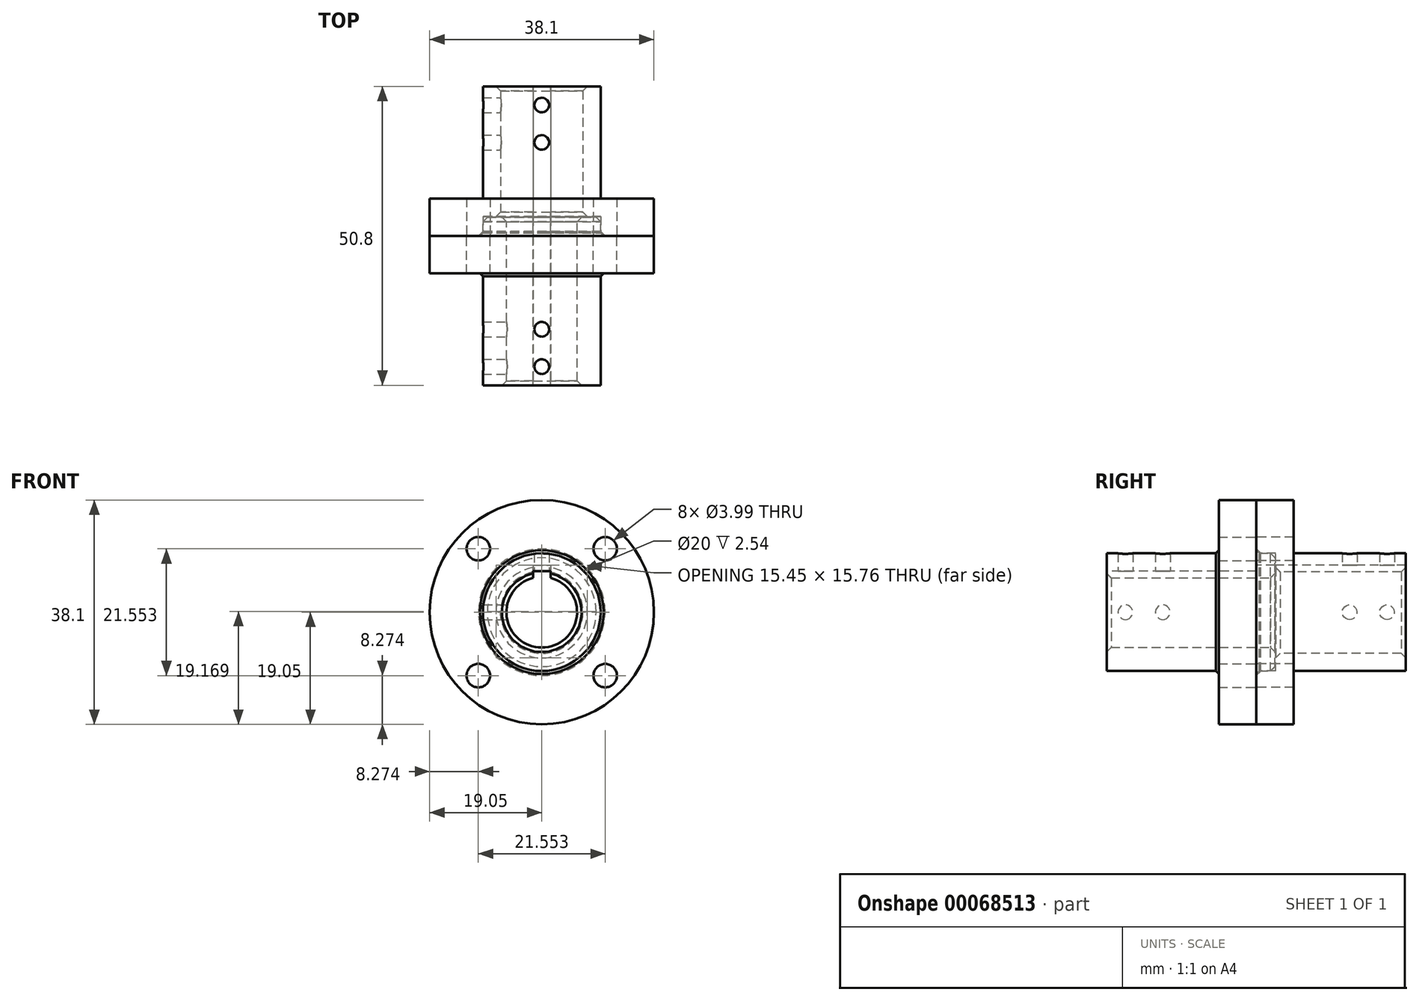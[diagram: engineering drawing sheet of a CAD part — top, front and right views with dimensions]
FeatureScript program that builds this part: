
annotation { "Feature Type Name" : "Feature", "Feature Type Description" : "" }
export const myFeature = defineFeature(function(context is Context, id is Id, definition is map)
    precondition{}
    {
        {
            var Q0;
            Q0=qCreatedBy(makeId("Front.planeOp"),FACE);
            var sketch = newSketch(context, id + "F0", { "sketchPlane" : qUnion([Q0])});
            skCircle(sketch, "E0", {"center": v(0, 0) * mm, "radius": 7 * mm});
            skCircle(sketch, "E1", {"center": v(0, 0) * mm, "radius": 6 * mm});
            skCircle(sketch, "E2", {"center": v(0, 0) * mm, "radius": 19.05 * mm});
            skCircle(sketch, "E3", {"center": v(-10.78, 10.78) * mm, "radius": 2 * mm});
            skCircle(sketch, "E4.1.0", {"center": v(-10.78, -10.78) * mm, "radius": 2 * mm});
            skCircle(sketch, "E4.2.0", {"center": v(10.78, -10.78) * mm, "radius": 2 * mm});
            skCircle(sketch, "E4.3.0", {"center": v(10.78, 10.78) * mm, "radius": 2 * mm});
            skCircle(sketch, "E5", {"center": v(0, 0) * mm, "radius": 10 * mm});
            skSolve(sketch);
        }
        {
            var Q0;
            Q0=qCreatedBy(makeId("Front.planeOp"),FACE);
            var sketch = newSketch(context, id + "F1", { "sketchPlane" : qUnion([Q0])});
            skLineSegment(sketch, "E6.bottom", {"start": v(0, 8) * mm, "end": v(-1.5, 8) * mm});
            skLineSegment(sketch, "E6.top", {"start": v(0, 3.58) * mm, "end": v(-1.5, 3.58) * mm});
            skLineSegment(sketch, "E6.left", {"start": v(0, 8) * mm, "end": v(0, 3.58) * mm, "construction": true});
            skLineSegment(sketch, "E6.right", {"start": v(-1.5, 8) * mm, "end": v(-1.5, 3.58) * mm});
            skLineSegment(sketch, "E7.MirrorCS", {"start": v(0, 8) * mm, "end": v(1.5, 8) * mm});
            skLineSegment(sketch, "E8.MirrorCS", {"start": v(1.5, 8) * mm, "end": v(1.5, 3.58) * mm});
            skLineSegment(sketch, "E9.MirrorCS", {"start": v(0, 3.58) * mm, "end": v(1.5, 3.58) * mm});
            skLineSegment(sketch, "E10", {"start": v(-1.5, 7) * mm, "end": v(1.5, 7) * mm});
            skSolve(sketch);
        }
        {
            var Q0;
            Q0=makeQuery(id+"F0.imprint","IMPRINT",FACE,{"disambiguationData":[TD([[makeQuery(id+"F0.imprint","IMPRINT",EDGE,{"derivedFrom":sQuery(id+"F0.wireOp",EDGE,"E0")}),-1.0]])]});
            var Q1;
            Q1=makeQuery(id+"F0.imprint","IMPRINT",FACE,{"disambiguationData":[TD([[makeQuery(id+"F0.imprint","IMPRINT",EDGE,{"derivedFrom":sQuery(id+"F0.wireOp",EDGE,"E2")}),1.0]])]});
            extrude(context, id + "F2", {"entities" : qUnion([Q0, Q1]), "depth" : 6.35 * mm});
        }
        {
            var Q0;
            Q0=makeQuery(id+"F0.imprint","IMPRINT",FACE,{"disambiguationData":[TD([[makeQuery(id+"F0.imprint","IMPRINT",EDGE,{"derivedFrom":sQuery(id+"F0.wireOp",EDGE,"E0")}),-1.0]])]});
            var Q1;
            Q1=makeQuery(id+"F0.imprint","IMPRINT",FACE,{"disambiguationData":[TD([[makeQuery(id+"F0.imprint","IMPRINT",EDGE,{"derivedFrom":sQuery(id+"F0.wireOp",EDGE,"E0")}),1.0]])]});
            extrude(context, id + "F3", {"entities" : qUnion([Q0, Q1]), "operationType" : NewBodyOperationType.ADD, "depth" : 25.4 * mm, "hasSecondDirection" : true, "secondDirectionOppositeDirection" : true, "secondDirectionDepth" : 3.17 * mm});
        }
        {
            var Q0;
            Q0=makeQuery(id+"F0.imprint","IMPRINT",FACE,{"disambiguationData":[TD([[makeQuery(id+"F0.imprint","IMPRINT",EDGE,{"derivedFrom":sQuery(id+"F0.wireOp",EDGE,"E2")}),1.0]])]});
            extrude(context, id + "F4", {"entities" : qUnion([Q0]), "oppositeDirection" : true, "depth" : 6.35 * mm});
        }
        {
            var Q0;
            Q0=makeQuery(id+"F0.imprint","IMPRINT",FACE,{"disambiguationData":[TD([[makeQuery(id+"F0.imprint","IMPRINT",EDGE,{"derivedFrom":sQuery(id+"F0.wireOp",EDGE,"E0")}),-1.0]])]});
            extrude(context, id + "F5", {"entities" : qUnion([Q0]), "operationType" : NewBodyOperationType.ADD, "oppositeDirection" : true, "depth" : 25.4 * mm, "hasSecondDirection" : true, "secondDirectionOppositeDirection" : true, "secondDirectionDepth" : 3.3 * mm});
        }
        {
            var Q0;
            Q0=makeQuery(id+"F3.boolean.opBoolean","INTERSECT",EDGE,{"derivedFrom":[makeQuery(id+"F2.opExtrude","CAP_FACE",FACE,{"disambiguationData":[OSD([sQuery(id+"F0.wireOp",EDGE,"E0"),sQuery(id+"F0.wireOp",EDGE,"E2"),sQuery(id+"F0.wireOp",EDGE,"E3"),sQuery(id+"F0.wireOp",EDGE,"E4.1.0"),sQuery(id+"F0.wireOp",EDGE,"E4.2.0"),sQuery(id+"F0.wireOp",EDGE,"E4.3.0")])],"isStart":false}),makeQuery(id+"F3.opExtrude","SWEPT_FACE",FACE,{"disambiguationData":[OSD([sQuery(id+"F0.wireOp",EDGE,"E5")])]})]});
            var Q1;
            Q1=makeQuery(id+"F4.opExtrude","CAP_EDGE",EDGE,{"disambiguationData":[OSD([sQuery(id+"F0.wireOp",EDGE,"E5")])],"isStart":false});
            var Q2;
            Q2=makeQuery(id+"F5.opExtrude","CAP_EDGE",EDGE,{"disambiguationData":[OSD([sQuery(id+"F0.wireOp",EDGE,"E5")])],"isStart":true});
            var Q3;
            Q3=makeQuery(id+"F3.boolean.opBoolean","INTERSECT",EDGE,{"derivedFrom":[makeQuery(id+"F2.opExtrude","CAP_FACE",FACE,{"disambiguationData":[OSD([sQuery(id+"F0.wireOp",EDGE,"E0"),sQuery(id+"F0.wireOp",EDGE,"E2"),sQuery(id+"F0.wireOp",EDGE,"E3"),sQuery(id+"F0.wireOp",EDGE,"E4.1.0"),sQuery(id+"F0.wireOp",EDGE,"E4.2.0"),sQuery(id+"F0.wireOp",EDGE,"E4.3.0")])],"isStart":true}),makeQuery(id+"F3.opExtrude","SWEPT_FACE",FACE,{"disambiguationData":[OSD([sQuery(id+"F0.wireOp",EDGE,"E5")])]})]});
            chamfer(context, id + "F6", {"entities" : qUnion([Q0, Q1, Q2, Q3]), "width" : 0.5 * mm, "tangentPropagation" : true});
        }
        {
            var Q0;
            Q0=makeQuery(id+"F4.opExtrude","CAP_EDGE",EDGE,{"disambiguationData":[OSD([sQuery(id+"F0.wireOp",EDGE,"E5")])],"isStart":true});
            var Q1;
            Q1=makeQuery(id+"F5.opExtrude","CAP_EDGE",EDGE,{"disambiguationData":[OSD([sQuery(id+"F0.wireOp",EDGE,"E0")])],"isStart":false});
            var Q2;
            Q2=makeQuery(id+"F5.opExtrude","CAP_EDGE",EDGE,{"disambiguationData":[OSD([sQuery(id+"F0.wireOp",EDGE,"E0")])],"isStart":true});
            var Q3;
            Q3=makeQuery(id+"F3.opExtrude","CAP_EDGE",EDGE,{"disambiguationData":[OSD([sQuery(id+"F0.wireOp",EDGE,"E1")])],"isStart":false});
            var Q4;
            Q4=makeQuery(id+"F3.opExtrude","CAP_EDGE",EDGE,{"disambiguationData":[OSD([sQuery(id+"F0.wireOp",EDGE,"E1")])],"isStart":true});
            var Q5;
            Q5=makeQuery(id+"F3.opExtrude","CAP_EDGE",EDGE,{"disambiguationData":[OSD([sQuery(id+"F0.wireOp",EDGE,"E5")])],"isStart":true});
            chamfer(context, id + "F7", {"entities" : qUnion([Q0, Q1, Q2, Q3, Q4, Q5]), "width" : 0.76 * mm, "tangentPropagation" : true});
        }
        {
            var Q0;
            {var subQ4=sQuery(id+"F1.wireOp",EDGE,"E6.top");Q0=makeQuery(id+"F1.imprint","IMPRINT",FACE,{"disambiguationData":[TD([[makeQuery(id+"F1.imprint","IMPRINT",EDGE,{"derivedFrom":subQ4}),-1.0]])]});}
            extrude(context, id + "F8", {"entities" : qUnion([Q0]), "operationType" : NewBodyOperationType.REMOVE, "oppositeDirection" : true, "depth" : 25.4 * mm, "hasSecondDirection" : true, "secondDirectionOppositeDirection" : false, "secondDirectionDepth" : 25.4 * mm});
        }
        {
            var Q0;
            {var subQ4=sQuery(id+"F1.wireOp",EDGE,"E6.top");Q0=makeQuery(id+"F1.imprint","IMPRINT",FACE,{"disambiguationData":[TD([[makeQuery(id+"F1.imprint","IMPRINT",EDGE,{"derivedFrom":subQ4}),-1.0]])]});}
            var Q1;
            {var subQ4=sQuery(id+"F1.wireOp",EDGE,"E6.bottom");Q1=makeQuery(id+"F1.imprint","IMPRINT",FACE,{"disambiguationData":[TD([[makeQuery(id+"F1.imprint","IMPRINT",EDGE,{"derivedFrom":subQ4}),1.0]])]});}
            extrude(context, id + "F9", {"entities" : qUnion([Q0, Q1]), "operationType" : NewBodyOperationType.REMOVE, "oppositeDirection" : true, "depth" : 25.4 * mm});
        }
        {
            var Q0;
            Q0=qCreatedBy(makeId("Top.planeOp"),FACE);
            var sketch = newSketch(context, id + "F10", { "sketchPlane" : qUnion([Q0])});
            skCircle(sketch, "E11", {"center": v(0, 15.88) * mm, "radius": 1.25 * mm});
            skCircle(sketch, "E12", {"center": v(0, 22.23) * mm, "radius": 1.25 * mm});
            skCircle(sketch, "E13", {"center": v(0, -15.88) * mm, "radius": 1.25 * mm});
            skCircle(sketch, "E14", {"center": v(0, -22.23) * mm, "radius": 1.25 * mm});
            skSolve(sketch);
        }
        {
            var Q0;
            Q0=qCreatedBy(makeId("Right.planeOp"),FACE);
            var sketch = newSketch(context, id + "F11", { "sketchPlane" : qUnion([Q0])});
            skPoint(sketch, "E15.0", {"position": v(-22.23, 0) * mm});
            skPoint(sketch, "E15.1", {"position": v(-15.88, 0) * mm});
            skPoint(sketch, "E15.2", {"position": v(15.88, 0) * mm});
            skPoint(sketch, "E15.3", {"position": v(22.23, 0) * mm});
            skCircle(sketch, "E16", {"center": v(-22.23, 0) * mm, "radius": 1.25 * mm});
            skCircle(sketch, "E17", {"center": v(-15.88, 0) * mm, "radius": 1.25 * mm});
            skCircle(sketch, "E18", {"center": v(15.88, 0) * mm, "radius": 1.25 * mm});
            skCircle(sketch, "E19", {"center": v(22.23, 0) * mm, "radius": 1.25 * mm});
            skLineSegment(sketch, "E20.0", {"start": v(20.98, 0) * mm, "end": v(23.48, 0) * mm, "construction": true});
            skSolve(sketch);
        }
        {
            var Q0;
            Q0 = qSketchRegion(id + "F10", true);
            extrude(context, id + "F12", {"entities" : qUnion([Q0]), "operationType" : NewBodyOperationType.REMOVE, "depth" : 25.4 * mm});
        }
        {
            var Q0;
            Q0 = qSketchRegion(id + "F11", true);
            extrude(context, id + "F13", {"entities" : qUnion([Q0]), "operationType" : NewBodyOperationType.REMOVE, "oppositeDirection" : true, "depth" : 25.4 * mm});
        }
    });
